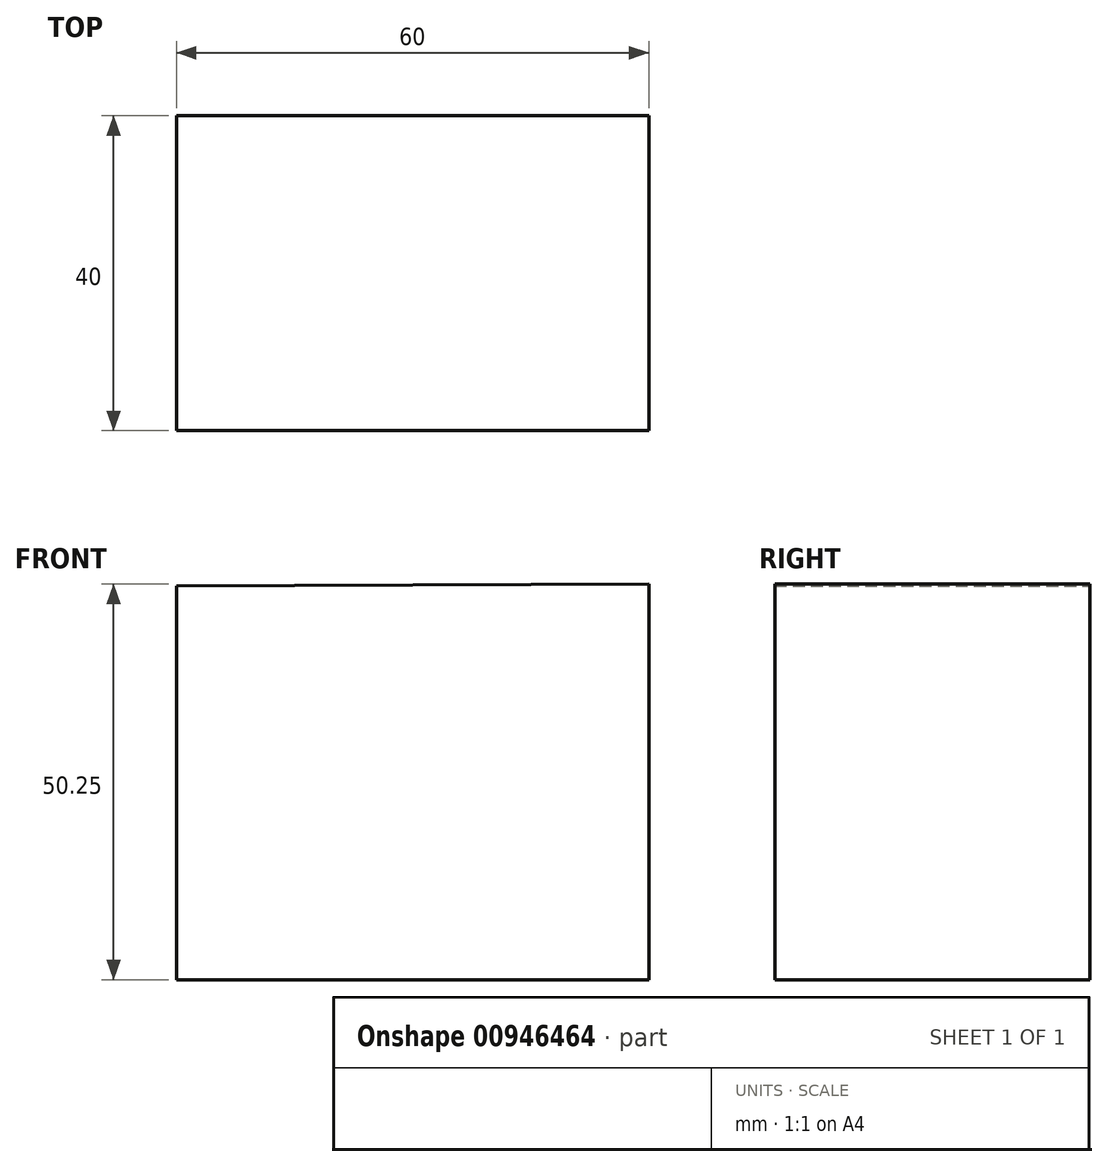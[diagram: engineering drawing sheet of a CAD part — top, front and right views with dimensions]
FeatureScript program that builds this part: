
annotation { "Feature Type Name" : "Feature", "Feature Type Description" : "" }
export const myFeature = defineFeature(function(context is Context, id is Id, definition is map)
    precondition{}
    {
        {
            var Q0;
            Q0=qCreatedBy(makeId("Front.planeOp"),FACE);
            var sketch = newSketch(context, id + "F0", { "sketchPlane" : qUnion([Q0])});
            skLineSegment(sketch, "E0", {"start": v(-30.12, 31.1) * mm, "end": v(-30.12, -18.9) * mm});
            skLineSegment(sketch, "E1", {"start": v(-30.12, -18.9) * mm, "end": v(29.88, -18.9) * mm});
            skLineSegment(sketch, "E2", {"start": v(29.88, -18.9) * mm, "end": v(29.88, 31.34) * mm});
            skLineSegment(sketch, "E3", {"start": v(-30.12, 31.1) * mm, "end": v(29.88, 31.34) * mm});
            skSolve(sketch);
        }
        {
            var Q0;
            Q0 = qSketchRegion(id + "F0", true);
            extrude(context, id + "F1", {"entities" : qUnion([Q0]), "depth" : 40 * mm, "offsetDistance" : 25 * mm});
        }
    });
